# Revit family: Distanzrohr VA
name_source: partatom
category: HLS-Bauteile
revit_build: Autodesk Revit 2017 (Build: 20190507_1515(x64)
units: mm (PartAtom-declared; Revit-internal decimal feet)

## family parameters
Arbeitsebenenbasiert = Nein
Beim Laden mit Abzugskörper schneiden = Nein
Bemaßung runder Anschluss = Durchmesser verwenden
Gemeinsam genutzt = Ja
Immer vertikal = Nein
Raumberechnungspunkt = Nein
Teiletyp = Normal

## types (2) — shared parameters
Fabrikat = MEFA
Kurztext2 = Länge 2000 mm
Länge = 2000 mm  [stored 6.56168 ft]
Material = Edelstahl
Mengeneinheit = m
Montagelänge = 2000 mm  [stored 6.56168 ft]

## per-type parameters (varying)
| type | Artikelnummer | D | D0 | EAN | Gewicht | Gewicht pro Bauteil | Gewicht pro Stück | Gewinde | Kurztext1 | vpe |
| Distanzrohr 1/2" L=2000, V4A | 0737002A4 | 21 mm  [stored 0.0688976 ft] | 16 mm  [stored 0.0524934 ft] | 4250928416964 | 1.15 kg | 2.30 kg | 2.30 kg | 1/2'' | Distanzrohr 1/2" V4A | 20 m |
| Distanzrohr 1" L=2000, V4A | 0737004A4 | 33 mm | 27 mm | 4250928416995 | 2.30 kg | 4.59 kg | 4.59 kg | 1'' | Distanzrohr 1" V4A | 10 m |

note: [stored X ft] marks values corroborated as IEEE doubles in the binary element streams (Revit-internal decimal feet)
